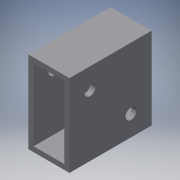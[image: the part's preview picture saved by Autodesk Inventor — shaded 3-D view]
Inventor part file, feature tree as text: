
AUTODESK INVENTOR PART (.ipt)
format: ipt  version: 2016 (Build 200138000, 138)  size: 109,568 bytes
history: native  units: in
note: dims shown in document units (in); Inventor stores cm internally (conversion verified against a paired STEP export)
features: extrude x2, sketch x2
ambient origin geometry x8: Origin, YZ Plane, XZ Plane, XY Plane, X Axis, Y Axis, Z Axis, Center Point
bodies: Solid1 (feature_tree)
feature tree (4):
  extrude  "Extrusion1"  Depth=2.0in
  extrude  "Extrusion2"  Depth=2.0in TaperAngle=0.0deg
  sketch  "Sketch1"  dims[d0=1.0in d1=2.0in]
  sketch  "Sketch2"  dims[d2=0.125in d3=2.0in d4=0.0in d5=0.2656in d6=0.2656in d7=0.5in d8=0.5in d9=0.5in d10=0.5in d11=1.0in d12=0.0in]
